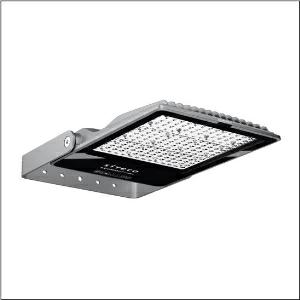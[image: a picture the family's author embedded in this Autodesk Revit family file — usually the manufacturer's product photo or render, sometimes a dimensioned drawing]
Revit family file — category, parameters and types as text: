
# Revit family: sicompact_r__31_midi___pl32_5xa7581d2k23_8dbf
name_source: partatom
category: Lighting Fixtures
units: mm (PartAtom-declared; Revit-internal decimal feet)

## family parameters
Cut with Voids When Loaded = No
Host = Face
Light Source = No
Part Type = Normal
Room Calculation Point = No
Round Connector Dimension = Use Diameter
Shared = No

## types (1)
- SiCompact® 31 midi  PL32 (1 x LED, 27000 lm, 165 W, 4000K)
    Apparent Load = 165 VA
    CIE Flux Codes = 32 69 98 100 100
    Color Rendering = 70
    Color Temperature = 4000K
    Default Elevation = 1800 mm
    Description = SiCompact® 31 midi, floodlight, primary light control with lens, of plastic, of toughened safety glass, transparent, light distribution: PL32, light emission: direct distribution, primary light characteristic: asymmetric, installation type: surface-mounted, LED, High Power LED, rated luminous flux: 27.000lm, luminous efficacy: 164lm/W, light colour: 740, colour temperature: 4000K, control gear: ECG, with cable, 3x 1.5mm², mains connection: 220..240V, AC, 50/60Hz, connection cable pre-assembled, cable length: 2m, rated input power: 165W, of diecast aluminium, specular, metallic grey (RAL 9006), length: 560mm, width: 330mm, height: 62mm, bracket, of sheet steel, coated, metallic grey (RAL 9006), ON/OFF, protection rating (complete): IP66, insulation class (complete): insulation class I (protective earthing), certification: CE, ENEC, impact resistance: IK08, permissible operating ambient temperature: -40..+45°C, packaging unit: 1 piece

Light Distribution: PL32
    Height = 62 mm  [stored 0.203412 ft]
    Lamp = 1 x LED
    Lamp Light Flux = 27000 lm
    Lamp Power = 165 W
    Lamp count = 1
    Length = 560 mm
    Luminous efficacy = 164 lm/W
    Manufacturer = Siteco
    ModVariant = No
    Model = 5XA7581D2K23
    Mounting Place = Wall
    Mounting Type = Surface mounted
    Number of Poles = 1
    OnlyDefault = Yes
    Power Factor = 1
    Product Name = SiCompact® 31 midi | PL32
    Product group = floodlight | wall mounted
    ProductGroupID = 2001
    Protection Class = Protection class I
    Protection Degree = IP 66
    RLX_Detail_Level = 1
    RLX_Emergency_Light_Flux = 0 lm
    RLX_Emergency_Type = 0
    RLX_Emergency_Type_DB = No
    RlxData = <blob elided: 98393 chars, md5=7e3bdcd6>
    Socket = socket
    Standby Power = 0 W
    System Light Flux = 27000 lm
    System Power = 165 W
    Type Comments = Product without accessories
    Type Image = l_1006415.jpg
    URL = http://relux.com
    VarID = ---
    Voltage = 0 V
    Weight = 0.00 kg
    Width = 333 mm

note: [stored X ft] marks values corroborated as IEEE doubles in the binary element streams (Revit-internal decimal feet)

## geometry (parser evidence)
native form markers: Blend x4, Sweep x12
no freeform markers — native parametric forms only
